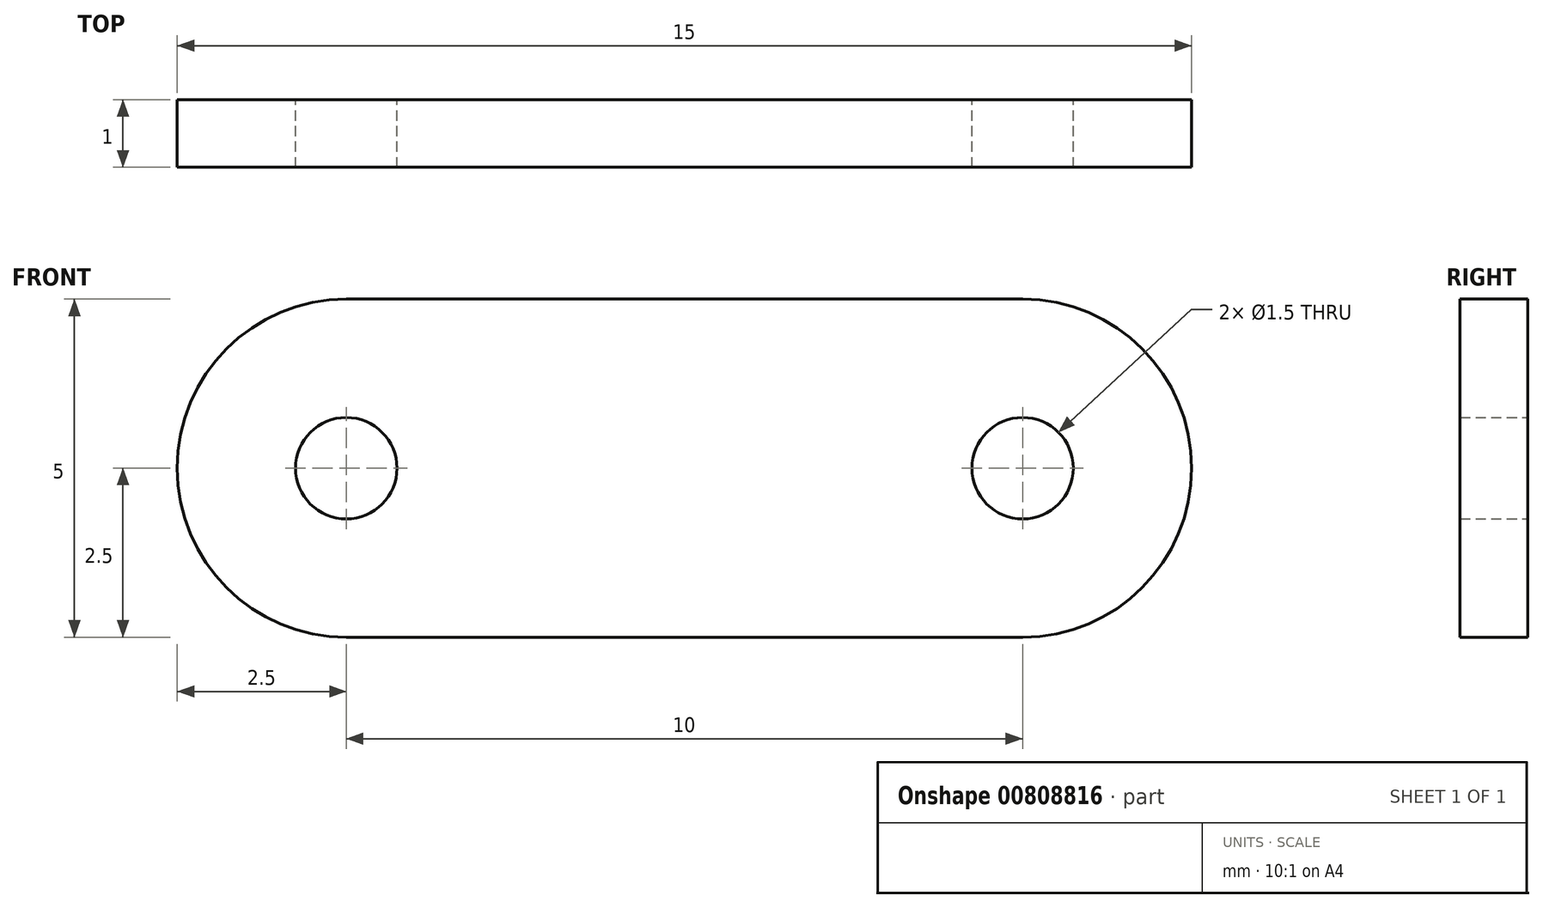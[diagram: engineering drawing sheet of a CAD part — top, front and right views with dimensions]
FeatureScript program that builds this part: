
annotation { "Feature Type Name" : "Feature", "Feature Type Description" : "" }
export const myFeature = defineFeature(function(context is Context, id is Id, definition is map)
    precondition{}
    {
        {
            var Q0;
            Q0=qCreatedBy(makeId("Front.planeOp"),FACE);
            var sketch = newSketch(context, id + "F0", { "sketchPlane" : qUnion([Q0])});
            skCircle(sketch, "E0", {"center": v(0, 0) * mm, "radius": 2.5 * mm});
            skCircle(sketch, "E1", {"center": v(10, 0) * mm, "radius": 2.5 * mm});
            skCircle(sketch, "E2", {"center": v(0, 0) * mm, "radius": 0.75 * mm});
            skCircle(sketch, "E3", {"center": v(10, 0) * mm, "radius": 0.75 * mm});
            skLineSegment(sketch, "E4", {"start": v(0, 2.5) * mm, "end": v(10, 2.5) * mm});
            skLineSegment(sketch, "E5", {"start": v(10, -2.5) * mm, "end": v(0, -2.5) * mm});
            skSolve(sketch);
        }
        {
            var Q0;
            Q0=makeQuery(id+"F0.imprint","IMPRINT",FACE,{"disambiguationData":[TD([[makeQuery(id+"F0.imprint","IMPRINT",EDGE,{"derivedFrom":sQuery(id+"F0.wireOp",EDGE,"E2")}),-1.0]])]});
            var Q1;
            Q1=makeQuery(id+"F0.imprint","IMPRINT",FACE,{"disambiguationData":[TD([[makeQuery(id+"F0.imprint","IMPRINT",EDGE,{"derivedFrom":sQuery(id+"F0.wireOp",EDGE,"E3")}),-1.0]])]});
            var Q2;
            {var subQ0=sQuery(id+"F0.wireOp",EDGE,"E4");Q2=makeQuery(id+"F0.imprint","IMPRINT",FACE,{"disambiguationData":[TD([[makeQuery(id+"F0.imprint","IMPRINT",EDGE,{"derivedFrom":subQ0}),-1.0]])]});}
            extrude(context, id + "F1", {"entities" : qUnion([Q0, Q1, Q2]), "depth" : 1 * mm, "offsetDistance" : 25 * mm});
        }
    });
